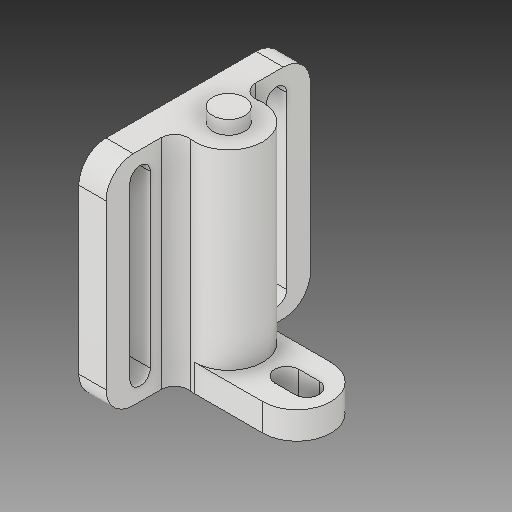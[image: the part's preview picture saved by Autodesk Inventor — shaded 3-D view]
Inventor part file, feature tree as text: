
AUTODESK INVENTOR PART (.ipt)
format: ipt  version: 2018.2 (Build 222227000, 227)  size: 184,832 bytes
history: native  units: mm
features: extrude x5, sketch x3, plane x2, fillet x2, projected_geometry x1
ambient origin geometry x8: Origin, YZ Plane, XZ Plane, XY Plane, X Axis, Y Axis, Z Axis, Center Point
bodies: Solid1 (feature_tree)
feature tree (13):
  sketch  "Sketch1"  dims[d0=4.7mm d1=10.0mm]
  extrude  "Extrusion1"  Depth=10.0mm
  extrude  "Extrusion2"  Depth=30.0mm TaperAngle=0.0deg
  extrude  "Extrusion3"  Depth=30.0mm
  plane  "Work Plane1"
  plane  "Work Plane2"
  extrude  "Extrusion4"  Depth=3.0mm
  extrude  "Extrusion5"  Depth=4.0mm TaperAngle=0.0deg
  fillet  "Fillet1"  Radius=2.0mm
  fillet  "Fillet2"  Radius=2.0mm
  sketch  "Sketch2"  dims[d5=2.0mm d6=0.0mm d7=30.0mm d8=0.0mm]
  projected_geometry  "Projected Loop1"
  sketch  "Sketch4"  dims[d9=32.0mm d10=0.0mm d11=30.0mm d12=15.0mm d13=4.0mm d14=0.0mm d26=-7.0mm d27=2.0mm d28=2.0mm d29=0.0mm d30=20.0mm d31=1.5mm d32=25.0mm d33=10.0mm d34=0.0mm d35=4.0mm d36=5.0mm d37=1.75mm d38=10.0mm d39=3.0mm]
